# Revit family: AudienceSystems_AuditoriumSeating_Espace628_CentreAisle
name_source: partatom
category: Furniture
revit_build: Autodesk Revit 2015 (Build: 20160220_1515(x64)
units: mm (PartAtom-declared; Revit-internal decimal feet)

## types (1)
- AudienceSystems_AuditoriumSeating_Espace628_CentreAisle
    Assembly Code = E2010500
    AssetType = Fixed
    BIMObjectName = BIMBox_AudienceSystems_AuditoriumSeating_Espace628CentreAisle
    Category = Pr_40_30_29_05: Auditorium Seating
    CodePerformance = Strength: certified to BS EN 12727:2000; Flammability: Upholstery fabric/foam comply with BS 5852 1990
    Color = <Primary Colour of Product>
    Constituents = Espace 628 Chair, Fixed Tier Seating, Centre Aisle
    Cost = 0 $
    Description = The Espace 628 is a classic, versatile chair suitable for use on fixed tiering, retractable platforms, or on the removable "Matrix" system.
    DurationUnit = Year
    ExpectedLife = 10
    Features = Self Tipping Design; Compact dimensions when closed; Suitable for use on min 260mm row rise/ 800mm row depth telescopic platforms; Wide range of options and enhancements
    Finish = Fabric Seat & Back; ABS Arm
    HighestSeatingHeight = 455 mm
    IfcExportAs = IfcFurnishingElementType
    IfcExportType = UNDEFINED
    Keynote = Pr_40_30_29_05
    LowestSeatingHeight = 445 mm  [stored 1.45997 ft]
    MainColor = <Primary Colour of Product>
    ManufacturerAddressUK = 19B Washington Road, West Wilts Trading Estate , Westbury, Wiltshire, BA13 4JP
    ManufacturerName = Audience Systems Ltd
    ManufacturerURL = www.audiencesystems.com
    Material = Seat: Polyurethane CMHR / CME foam, Backrest: Polyurethane CMHR / CME foam, Arm: ABS Injection Moulding
    Model = Espace628
    ModelNumber = Espace628
    ModelReference = Espace628withCentralAisle
    NBSDescription = Auditoria fittings, furnishings and equipment system
    NBSReference = 35-15-05/105
    Name = AuditoriumSeating_Espace628withCentreAisle_AudienceSystems
    ProductInformation = www.audiencesystems.com/product/espace-628?filterSlugQuery=all
    ScheduleType |RF| = IfcFurnitureSeating
    Shape = Various
    Size = Please refer to Nominal Dimensions for overall size of Auditorium Seating
    Style = Auditorium Seating
    URL = www.audiencesystems.com
    Uniclass2015Description = Auditorium Seating
    Uniclass2015Reference = Pr_40_30_29_05
    Uniclass2015Version = Products v1.1
    Version = 1
    WarrantyDurationLabor = 10
    WarrantyDurationParts = 10
    WarrantyDurationUnit = Year

note: [stored X ft] marks values corroborated as IEEE doubles in the binary element streams (Revit-internal decimal feet)

## geometry (parser evidence)
native form markers: Sweep x24
no freeform markers — native parametric forms only
